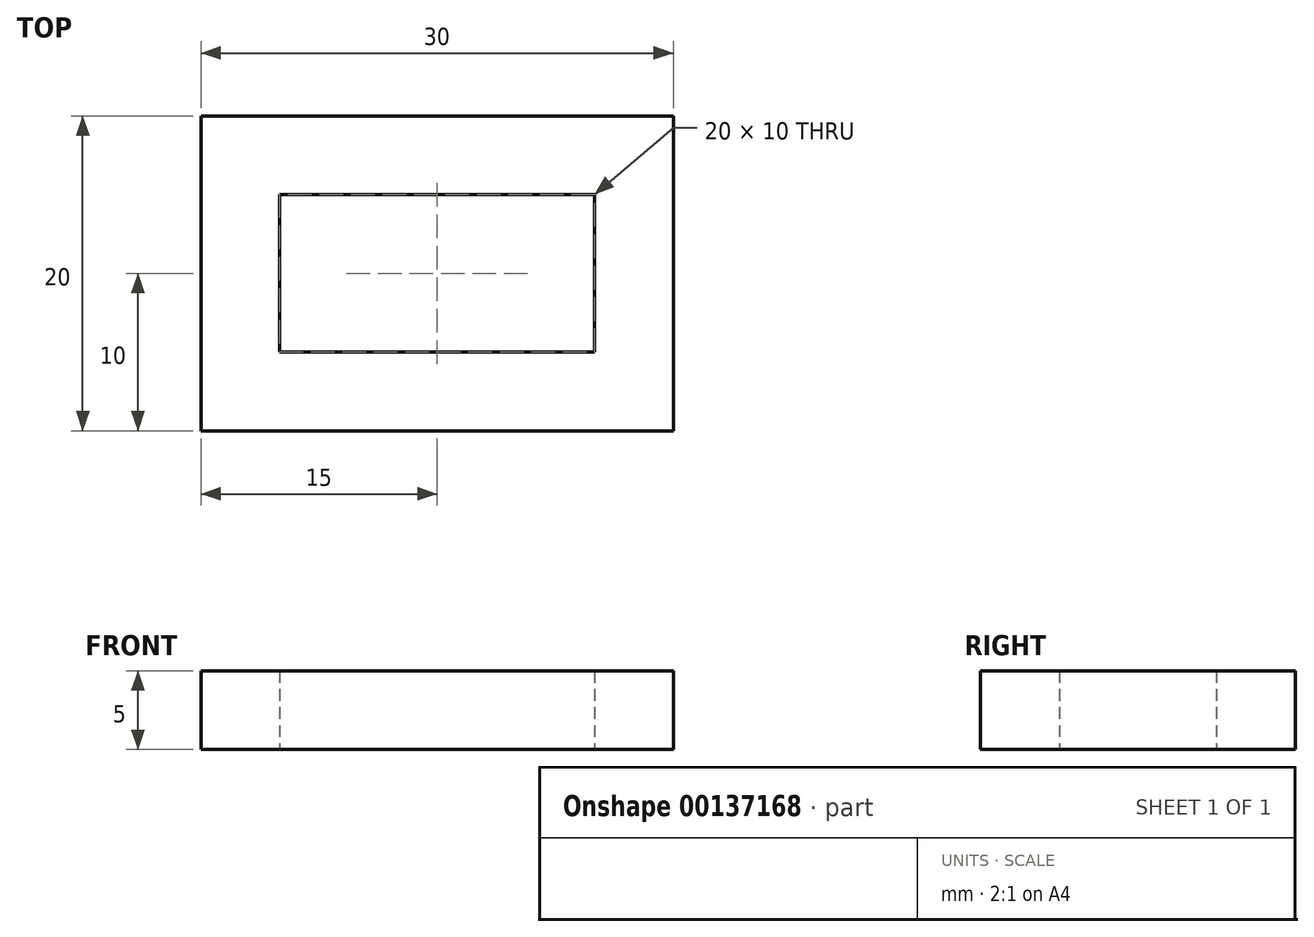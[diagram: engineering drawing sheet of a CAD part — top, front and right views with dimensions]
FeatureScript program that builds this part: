
annotation { "Feature Type Name" : "Feature", "Feature Type Description" : "" }
export const myFeature = defineFeature(function(context is Context, id is Id, definition is map)
    precondition{}
    {
        {
            var Q0;
            Q0=qCreatedBy(makeId("Top.planeOp"),FACE);
            var sketch = newSketch(context, id + "F0", { "sketchPlane" : qUnion([Q0])});
            skLineSegment(sketch, "E0.bottom", {"start": v(15, 10) * mm, "end": v(-15, 10) * mm});
            skLineSegment(sketch, "E0.top", {"start": v(15, -10) * mm, "end": v(-15, -10) * mm});
            skLineSegment(sketch, "E0.left", {"start": v(15, 10) * mm, "end": v(15, -10) * mm});
            skLineSegment(sketch, "E0.right", {"start": v(-15, 10) * mm, "end": v(-15, -10) * mm});
            skPoint(sketch, "E0.middle", {"position": v(0, 0) * mm});
            skLineSegment(sketch, "E1.bottom", {"start": v(10, 5) * mm, "end": v(-10, 5) * mm});
            skLineSegment(sketch, "E1.top", {"start": v(10, -5) * mm, "end": v(-10, -5) * mm});
            skLineSegment(sketch, "E1.left", {"start": v(10, 5) * mm, "end": v(10, -5) * mm});
            skLineSegment(sketch, "E1.right", {"start": v(-10, 5) * mm, "end": v(-10, -5) * mm});
            skSolve(sketch);
        }
        {
            var Q0;
            Q0 = qSketchRegion(id + "F0", true);
            extrude(context, id + "F1", {"entities" : qUnion([Q0]), "depth" : 5 * mm});
        }
    });
